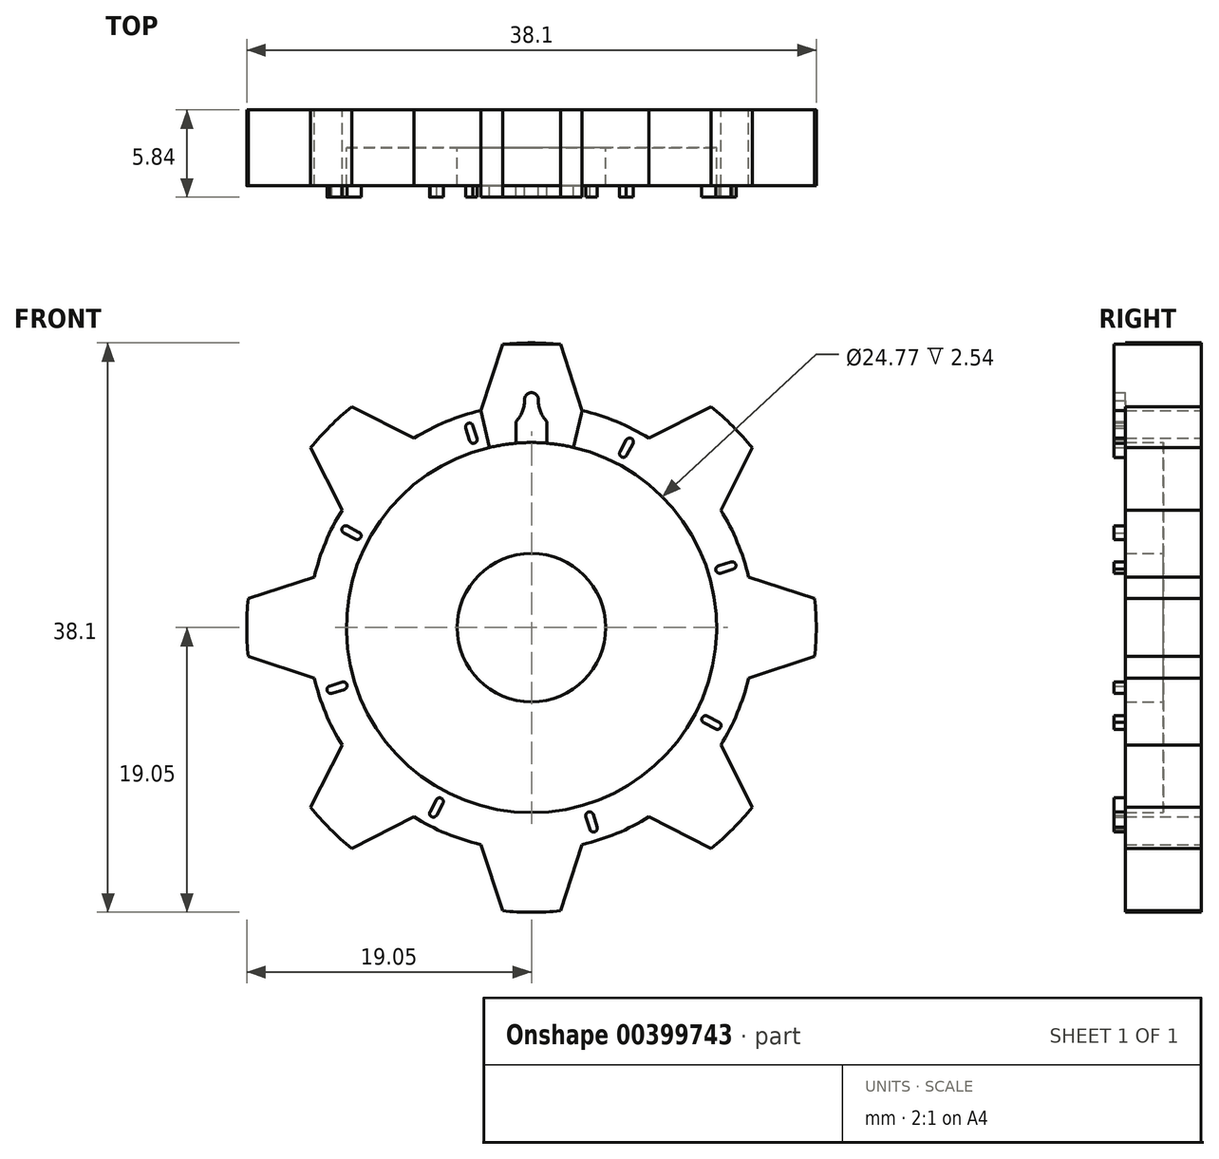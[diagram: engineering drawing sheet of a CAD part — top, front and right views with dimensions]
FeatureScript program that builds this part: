
annotation { "Feature Type Name" : "Feature", "Feature Type Description" : "" }
export const myFeature = defineFeature(function(context is Context, id is Id, definition is map)
    precondition{}
    {
        {
            var Q0;
            Q0=qCreatedBy(makeId("Front.planeOp"),FACE);
            var sketch = newSketch(context, id + "F0", { "sketchPlane" : qUnion([Q0])});
            skCircle(sketch, "E0", {"center": v(0, 0) * mm, "radius": 19.05 * mm});
            skLineSegment(sketch, "E1", {"start": v(-1.9, 19.05) * mm, "end": v(1.9, 19.05) * mm});
            skPoint(sketch, "E2", {"position": v(0, 19.05) * mm});
            skLineSegment(sketch, "E3.1.0", {"start": v(-14.82, 12.12) * mm, "end": v(-12.12, 14.82) * mm});
            skLineSegment(sketch, "E3.2.0", {"start": v(-19.05, -1.9) * mm, "end": v(-19.05, 1.9) * mm});
            skLineSegment(sketch, "E4.1.3.0", {"start": v(-12.12, -14.82) * mm, "end": v(-14.82, -12.12) * mm});
            skLineSegment(sketch, "E4.1.4.0", {"start": v(1.9, -19.05) * mm, "end": v(-1.9, -19.05) * mm});
            skLineSegment(sketch, "E4.1.5.0", {"start": v(14.82, -12.12) * mm, "end": v(12.12, -14.82) * mm});
            skLineSegment(sketch, "E4.1.6.0", {"start": v(19.05, 1.9) * mm, "end": v(19.05, -1.9) * mm});
            skLineSegment(sketch, "E4.1.7.0", {"start": v(12.12, 14.82) * mm, "end": v(14.82, 12.12) * mm});
            skCircle(sketch, "E5", {"center": v(0, 0) * mm, "radius": 14.91 * mm});
            skLineSegment(sketch, "E6", {"start": v(-1.9, 19.05) * mm, "end": v(-3.4, 14.52) * mm});
            skLineSegment(sketch, "E7", {"start": v(0, 0) * mm, "end": v(0, 23.52) * mm});
            skLineSegment(sketch, "E8.MirrorCS", {"start": v(1.9, 19.05) * mm, "end": v(3.4, 14.52) * mm});
            skLineSegment(sketch, "E9.1.0", {"start": v(-14.82, 12.12) * mm, "end": v(-12.67, 7.87) * mm});
            skLineSegment(sketch, "E9.1.1", {"start": v(-12.12, 14.82) * mm, "end": v(-7.87, 12.67) * mm});
            skLineSegment(sketch, "E9.2.0", {"start": v(-19.05, -1.9) * mm, "end": v(-14.52, -3.4) * mm});
            skLineSegment(sketch, "E9.2.1", {"start": v(-19.05, 1.9) * mm, "end": v(-14.52, 3.4) * mm});
            skLineSegment(sketch, "E9.3.0", {"start": v(-12.12, -14.82) * mm, "end": v(-7.87, -12.67) * mm});
            skLineSegment(sketch, "E9.3.1", {"start": v(-14.82, -12.12) * mm, "end": v(-12.67, -7.87) * mm});
            skLineSegment(sketch, "E9.4.0", {"start": v(1.9, -19.05) * mm, "end": v(3.4, -14.52) * mm});
            skLineSegment(sketch, "E9.4.1", {"start": v(-1.9, -19.05) * mm, "end": v(-3.4, -14.52) * mm});
            skLineSegment(sketch, "E9.5.0", {"start": v(14.82, -12.12) * mm, "end": v(12.67, -7.87) * mm});
            skLineSegment(sketch, "E9.5.1", {"start": v(12.12, -14.82) * mm, "end": v(7.87, -12.67) * mm});
            skLineSegment(sketch, "E9.6.0", {"start": v(19.05, 1.9) * mm, "end": v(14.52, 3.4) * mm});
            skLineSegment(sketch, "E9.6.1", {"start": v(19.05, -1.9) * mm, "end": v(14.52, -3.4) * mm});
            skLineSegment(sketch, "E9.7.0", {"start": v(12.12, 14.82) * mm, "end": v(7.87, 12.67) * mm});
            skLineSegment(sketch, "E9.7.1", {"start": v(14.82, 12.12) * mm, "end": v(12.67, 7.87) * mm});
            skSolve(sketch);
        }
        {
            var Q0;
            {var subQ3=sQuery(id+"F0.wireOp",EDGE,"E9.1.1");var subQ5=sQuery(id+"F0.wireOp",EDGE,"E0");var subQ8=makeQuery(id+"F0.imprint","INTERSECT",VERTEX,{"derivedFrom":[subQ5,subQ3]});Q0=makeQuery(id+"F0.imprint","IMPRINT",FACE,{"disambiguationData":[TD([[makeQuery(id+"F0.imprint","IMPRINT",EDGE,{"disambiguationData":[TD([[subQ8,-1.0]])],"derivedFrom":subQ5}),1.0]])]});}
            var Q1;
            {var subQ3=sQuery(id+"F0.wireOp",EDGE,"E9.7.1");var subQ5=sQuery(id+"F0.wireOp",EDGE,"E0");var subQ8=makeQuery(id+"F0.imprint","INTERSECT",VERTEX,{"derivedFrom":[subQ5,subQ3]});Q1=makeQuery(id+"F0.imprint","IMPRINT",FACE,{"disambiguationData":[TD([[makeQuery(id+"F0.imprint","IMPRINT",EDGE,{"disambiguationData":[TD([[subQ8,-1.0]])],"derivedFrom":subQ5}),1.0]])]});}
            var Q2;
            {var subQ0=sQuery(id+"F0.wireOp",EDGE,"E9.6.0");var subQ5=sQuery(id+"F0.wireOp",EDGE,"E0");var subQ8=makeQuery(id+"F0.imprint","INTERSECT",VERTEX,{"derivedFrom":[subQ5,subQ0]});Q2=makeQuery(id+"F0.imprint","IMPRINT",FACE,{"disambiguationData":[TD([[makeQuery(id+"F0.imprint","IMPRINT",EDGE,{"disambiguationData":[TD([[subQ8,1.0]])],"derivedFrom":subQ5}),1.0]])]});}
            var Q3;
            {var subQ0=sQuery(id+"F0.wireOp",EDGE,"E8.MirrorCS");var subQ5=sQuery(id+"F0.wireOp",EDGE,"E5");var subQ6=makeQuery(id+"F0.imprint","INTERSECT",VERTEX,{"derivedFrom":[subQ5,subQ0]});Q3=makeQuery(id+"F0.imprint","IMPRINT",FACE,{"disambiguationData":[TD([[makeQuery(id+"F0.imprint","IMPRINT",EDGE,{"disambiguationData":[TD([[subQ6,-1.0]])],"derivedFrom":subQ5}),-1.0]])]});}
            var Q4;
            {var subQ0=sQuery(id+"F0.wireOp",EDGE,"E6");var subQ5=sQuery(id+"F0.wireOp",EDGE,"E5");var subQ6=makeQuery(id+"F0.imprint","INTERSECT",VERTEX,{"derivedFrom":[subQ5,subQ0]});Q4=makeQuery(id+"F0.imprint","IMPRINT",FACE,{"disambiguationData":[TD([[makeQuery(id+"F0.imprint","IMPRINT",EDGE,{"disambiguationData":[TD([[subQ6,1.0]])],"derivedFrom":subQ5}),-1.0]])]});}
            var Q5;
            {var subQ3=sQuery(id+"F0.wireOp",EDGE,"E9.2.1");var subQ5=sQuery(id+"F0.wireOp",EDGE,"E0");var subQ8=makeQuery(id+"F0.imprint","INTERSECT",VERTEX,{"derivedFrom":[subQ5,subQ3]});Q5=makeQuery(id+"F0.imprint","IMPRINT",FACE,{"disambiguationData":[TD([[makeQuery(id+"F0.imprint","IMPRINT",EDGE,{"disambiguationData":[TD([[subQ8,-1.0]])],"derivedFrom":subQ5}),1.0]])]});}
            var Q6;
            {var subQ3=sQuery(id+"F0.wireOp",EDGE,"E0");var subQ5=sQuery(id+"F0.wireOp",EDGE,"E9.3.1");var subQ8=makeQuery(id+"F0.imprint","INTERSECT",VERTEX,{"derivedFrom":[subQ3,subQ5]});Q6=makeQuery(id+"F0.imprint","IMPRINT",FACE,{"disambiguationData":[TD([[makeQuery(id+"F0.imprint","IMPRINT",EDGE,{"disambiguationData":[TD([[subQ8,-1.0]])],"derivedFrom":subQ3}),1.0]])]});}
            var Q7;
            {var subQ3=sQuery(id+"F0.wireOp",EDGE,"E0");var subQ6=sQuery(id+"F0.wireOp",EDGE,"E9.4.1");var subQ8=makeQuery(id+"F0.imprint","INTERSECT",VERTEX,{"derivedFrom":[subQ3,subQ6]});Q7=makeQuery(id+"F0.imprint","IMPRINT",FACE,{"disambiguationData":[TD([[makeQuery(id+"F0.imprint","IMPRINT",EDGE,{"disambiguationData":[TD([[subQ8,-1.0]])],"derivedFrom":subQ3}),1.0]])]});}
            var Q8;
            {var subQ3=sQuery(id+"F0.wireOp",EDGE,"E0");var subQ5=sQuery(id+"F0.wireOp",EDGE,"E9.5.1");var subQ8=makeQuery(id+"F0.imprint","INTERSECT",VERTEX,{"derivedFrom":[subQ3,subQ5]});Q8=makeQuery(id+"F0.imprint","IMPRINT",FACE,{"disambiguationData":[TD([[makeQuery(id+"F0.imprint","IMPRINT",EDGE,{"disambiguationData":[TD([[subQ8,-1.0]])],"derivedFrom":subQ3}),1.0]])]});}
            var Q9;
            {var subQ0=sQuery(id+"F0.wireOp",EDGE,"E5");var subQ8=makeQuery(id+"F0.imprint","INTERSECT",VERTEX,{"derivedFrom":[subQ0,sQuery(id+"F0.wireOp",EDGE,"E9.6.0")]});Q9=makeQuery(id+"F0.imprint","IMPRINT",FACE,{"disambiguationData":[TD([[makeQuery(id+"F0.imprint","IMPRINT",EDGE,{"disambiguationData":[TD([[subQ8,-1.0]])],"derivedFrom":subQ0}),1.0]])]});}
            extrude(context, id + "F1", {"entities" : qUnion([Q0, Q1, Q2, Q3, Q4, Q5, Q6, Q7, Q8, Q9]), "depth" : 2.54 * mm});
        }
        {
            var Q0;
            Q0=makeQuery(id+"F1.opExtrude","CAP_FACE",FACE,{"disambiguationData":[OSD([sQuery(id+"F0.wireOp",EDGE,"E0"),sQuery(id+"F0.wireOp",EDGE,"E5"),sQuery(id+"F0.wireOp",EDGE,"E6"),sQuery(id+"F0.wireOp",EDGE,"E8.MirrorCS"),sQuery(id+"F0.wireOp",EDGE,"E9.1.0"),sQuery(id+"F0.wireOp",EDGE,"E9.1.1"),sQuery(id+"F0.wireOp",EDGE,"E9.2.0"),sQuery(id+"F0.wireOp",EDGE,"E9.2.1"),sQuery(id+"F0.wireOp",EDGE,"E9.3.0"),sQuery(id+"F0.wireOp",EDGE,"E9.3.1"),sQuery(id+"F0.wireOp",EDGE,"E9.4.0"),sQuery(id+"F0.wireOp",EDGE,"E9.4.1"),sQuery(id+"F0.wireOp",EDGE,"E9.5.0"),sQuery(id+"F0.wireOp",EDGE,"E9.5.1"),sQuery(id+"F0.wireOp",EDGE,"E9.6.0"),sQuery(id+"F0.wireOp",EDGE,"E9.6.1"),sQuery(id+"F0.wireOp",EDGE,"E9.7.0"),sQuery(id+"F0.wireOp",EDGE,"E9.7.1")])],"isStart":false});
            var sketch = newSketch(context, id + "F2", { "sketchPlane" : qUnion([Q0])});
            skCircle(sketch, "E10", {"center": v(0, 0) * mm, "radius": 12.38 * mm});
            skCircle(sketch, "E11", {"center": v(0, 0) * mm, "radius": 4.97 * mm});
            skSolve(sketch);
        }
        {
            var Q0;
            Q0=makeQuery(id+"F2.imprint","IMPRINT",FACE,{"disambiguationData":[TD([[makeQuery(id+"F2.imprint","IMPRINT",EDGE,{"derivedFrom":sQuery(id+"F2.wireOp",EDGE,"E10")}),-1.0]])]});
            var Q1;
            Q1=makeQuery(id+"F2.imprint","IMPRINT",FACE,{"disambiguationData":[TD([[makeQuery(id+"F2.imprint","IMPRINT",EDGE,{"derivedFrom":sQuery(id+"F2.wireOp",EDGE,"E11")}),1.0]])]});
            extrude(context, id + "F3", {"entities" : qUnion([Q0, Q1]), "operationType" : NewBodyOperationType.ADD, "depth" : 2.54 * mm});
        }
        {
            var Q0;
            Q0=makeQuery(id+"F3.opExtrude","CAP_FACE",FACE,{"disambiguationData":[OSD([sQuery(id+"F2.wireOp",EDGE,"E11")])],"isStart":false});
            var sketch = newSketch(context, id + "F4", { "sketchPlane" : qUnion([Q0])});
            skCircle(sketch, "E12", {"center": v(0, 0) * mm, "radius": 2.8 * mm});
            skPoint(sketch, "E13", {"position": v(-1.94, 18.95) * mm});
            skPoint(sketch, "E14", {"position": v(1.94, 18.95) * mm});
            skPoint(sketch, "E15", {"position": v(-3.4, 14.52) * mm});
            skPoint(sketch, "E16", {"position": v(3.4, 14.52) * mm});
            skLineSegment(sketch, "E17", {"start": v(-3.4, 14.52) * mm, "end": v(-1.94, 18.95) * mm});
            skLineSegment(sketch, "E18", {"start": v(1.94, 18.95) * mm, "end": v(3.4, 14.52) * mm});
            skLineSegment(sketch, "E19", {"start": v(-3.4, 14.52) * mm, "end": v(-2.81, 12.05) * mm});
            skLineSegment(sketch, "E20", {"start": v(3.4, 14.52) * mm, "end": v(2.8, 12.06) * mm});
            skArc(sketch, "E21", {"start": v(2.8, 12.06) * mm, "mid": v(1.91, 12.23) * mm, "end": v(1, 12.33) * mm});
            skLineSegment(sketch, "E22", {"start": v(-1.94, 18.95) * mm, "end": v(1.94, 18.95) * mm});
            skLineSegment(sketch, "E23", {"start": v(0, 0) * mm, "end": v(0, 11.5) * mm, "construction": true});
            skPoint(sketch, "E23.endSnap0", {"position": v(0, 12.37) * mm});
            skArc(sketch, "E24", {"start": v(-3.9, 13.49) * mm, "mid": v(-4.22, 13.67) * mm, "end": v(-4.4, 13.35) * mm});
            skArc(sketch, "E25", {"start": v(-4.13, 12.5) * mm, "mid": v(-3.81, 12.34) * mm, "end": v(-3.65, 12.66) * mm});
            skLineSegment(sketch, "E26", {"start": v(0, 0) * mm, "end": v(-4.15, 13.43) * mm, "construction": true});
            skLineSegment(sketch, "E27", {"start": v(-4.4, 13.35) * mm, "end": v(-4.13, 12.5) * mm});
            skLineSegment(sketch, "E28", {"start": v(-3.91, 13.52) * mm, "end": v(-3.65, 12.66) * mm});
            skLineSegment(sketch, "E29.MirrorCS", {"start": v(3.91, 13.52) * mm, "end": v(3.65, 12.66) * mm});
            skArc(sketch, "E30.MirrorCS", {"start": v(3.9, 13.49) * mm, "mid": v(4.22, 13.67) * mm, "end": v(4.4, 13.35) * mm});
            skArc(sketch, "E31.MirrorCS", {"start": v(4.13, 12.5) * mm, "mid": v(3.81, 12.34) * mm, "end": v(3.65, 12.66) * mm});
            skLineSegment(sketch, "E32.MirrorCS", {"start": v(4.4, 13.35) * mm, "end": v(4.13, 12.5) * mm});
            skArc(sketch, "E33", {"start": v(0.46, 15.2) * mm, "mid": v(0, 15.72) * mm, "end": v(-0.46, 15.2) * mm});
            skLineSegment(sketch, "E34", {"start": v(1, 13.79) * mm, "end": v(1, 12.33) * mm});
            skLineSegment(sketch, "E35", {"start": v(-1.03, 13.79) * mm, "end": v(-1.03, 12.33) * mm});
            skArc(sketch, "E36", {"start": v(-1.03, 13.79) * mm, "mid": v(-0.6, 14.48) * mm, "end": v(-0.46, 15.3) * mm});
            skArc(sketch, "E37.MirrorCS", {"start": v(1.03, 13.79) * mm, "mid": v(0.6, 14.48) * mm, "end": v(0.46, 15.3) * mm});
            skPoint(sketch, "E38.start.orphan", {"position": v(0, 13.79) * mm});
            skArc(sketch, "E39.trimOffspring", {"start": v(-1.03, 12.33) * mm, "mid": v(-1.93, 12.22) * mm, "end": v(-2.81, 12.05) * mm});
            skLineSegment(sketch, "E40.MirrorCS", {"start": v(1.03, 13.79) * mm, "end": v(1.03, 12.33) * mm});
            skArc(sketch, "E41.MirrorCS", {"start": v(1.03, 12.33) * mm, "mid": v(1.92, 12.22) * mm, "end": v(2.81, 12.05) * mm});
            skLineSegment(sketch, "E42.MirrorCS", {"start": v(3.4, 14.52) * mm, "end": v(2.81, 12.05) * mm});
            skLineSegment(sketch, "E43.MirrorCS", {"start": v(3.4, 14.52) * mm, "end": v(1.94, 18.95) * mm});
            skArc(sketch, "E44.MirrorCS", {"start": v(-0.46, 15.2) * mm, "mid": v(0, 15.72) * mm, "end": v(0.46, 15.2) * mm});
            skLineSegment(sketch, "E45.1.0", {"start": v(-12.55, 6.34) * mm, "end": v(-11.77, 5.92) * mm});
            skArc(sketch, "E45.1.1", {"start": v(-12.3, 6.78) * mm, "mid": v(-12.65, 6.69) * mm, "end": v(-12.55, 6.34) * mm});
            skLineSegment(sketch, "E45.1.2", {"start": v(-12.33, 6.8) * mm, "end": v(-11.53, 6.37) * mm});
            skArc(sketch, "E45.1.3", {"start": v(-11.77, 5.92) * mm, "mid": v(-11.42, 6.03) * mm, "end": v(-11.53, 6.37) * mm});
            skLineSegment(sketch, "E45.1.4", {"start": v(-12.67, 7.87) * mm, "end": v(-10.51, 6.53) * mm});
            skArc(sketch, "E45.1.5", {"start": v(-9.45, 8) * mm, "mid": v(-10, 7.28) * mm, "end": v(-10.51, 6.53) * mm});
            skLineSegment(sketch, "E45.1.6", {"start": v(-10.47, 9.02) * mm, "end": v(-9.45, 8) * mm});
            skArc(sketch, "E45.1.7", {"start": v(-10.47, 9.02) * mm, "mid": v(-10.66, 9.82) * mm, "end": v(-11.14, 10.49) * mm});
            skArc(sketch, "E45.1.8", {"start": v(-10.42, 11.07) * mm, "mid": v(-11.11, 11.12) * mm, "end": v(-11.08, 10.42) * mm});
            skArc(sketch, "E45.1.9", {"start": v(-9.02, 10.47) * mm, "mid": v(-9.82, 10.66) * mm, "end": v(-10.49, 11.14) * mm});
            skLineSegment(sketch, "E45.1.10", {"start": v(-9.02, 10.47) * mm, "end": v(-8, 9.44) * mm});
            skArc(sketch, "E45.1.11", {"start": v(-8, 9.44) * mm, "mid": v(-7.28, 10) * mm, "end": v(-6.53, 10.51) * mm});
            skLineSegment(sketch, "E45.1.12", {"start": v(-7.87, 12.67) * mm, "end": v(-6.54, 10.5) * mm});
            skArc(sketch, "E45.1.13", {"start": v(-5.92, 11.77) * mm, "mid": v(-6.03, 11.42) * mm, "end": v(-6.37, 11.53) * mm});
            skArc(sketch, "E45.1.14", {"start": v(-6.78, 12.3) * mm, "mid": v(-6.69, 12.65) * mm, "end": v(-6.34, 12.55) * mm});
            skLineSegment(sketch, "E45.1.15", {"start": v(-6.34, 12.55) * mm, "end": v(-5.92, 11.77) * mm});
            skLineSegment(sketch, "E45.1.16", {"start": v(-6.8, 12.33) * mm, "end": v(-6.37, 11.53) * mm});
            skLineSegment(sketch, "E45.1.17", {"start": v(-7.87, 12.67) * mm, "end": v(-12.03, 14.77) * mm});
            skLineSegment(sketch, "E45.1.18", {"start": v(-14.77, 12.03) * mm, "end": v(-12.03, 14.77) * mm});
            skLineSegment(sketch, "E45.1.19", {"start": v(-12.67, 7.87) * mm, "end": v(-14.77, 12.03) * mm});
            skLineSegment(sketch, "E45.2.0", {"start": v(-13.35, -4.4) * mm, "end": v(-12.5, -4.13) * mm});
            skArc(sketch, "E45.2.1", {"start": v(-13.49, -3.9) * mm, "mid": v(-13.67, -4.22) * mm, "end": v(-13.35, -4.4) * mm});
            skLineSegment(sketch, "E45.2.2", {"start": v(-13.52, -3.91) * mm, "end": v(-12.66, -3.65) * mm});
            skArc(sketch, "E45.2.3", {"start": v(-12.5, -4.13) * mm, "mid": v(-12.34, -3.81) * mm, "end": v(-12.66, -3.65) * mm});
            skLineSegment(sketch, "E45.2.4", {"start": v(-14.52, -3.4) * mm, "end": v(-12.05, -2.81) * mm});
            skArc(sketch, "E45.2.5", {"start": v(-12.33, -1.03) * mm, "mid": v(-12.22, -1.93) * mm, "end": v(-12.05, -2.81) * mm});
            skLineSegment(sketch, "E45.2.6", {"start": v(-13.79, -1.03) * mm, "end": v(-12.33, -1.03) * mm});
            skArc(sketch, "E45.2.7", {"start": v(-13.79, -1.03) * mm, "mid": v(-14.48, -0.6) * mm, "end": v(-15.3, -0.46) * mm});
            skArc(sketch, "E45.2.8", {"start": v(-15.2, 0.46) * mm, "mid": v(-15.72, 0) * mm, "end": v(-15.2, -0.46) * mm});
            skArc(sketch, "E45.2.9", {"start": v(-13.79, 1.03) * mm, "mid": v(-14.48, 0.6) * mm, "end": v(-15.3, 0.46) * mm});
            skLineSegment(sketch, "E45.2.10", {"start": v(-13.79, 1.03) * mm, "end": v(-12.33, 1.03) * mm});
            skArc(sketch, "E45.2.11", {"start": v(-12.33, 1.03) * mm, "mid": v(-12.22, 1.92) * mm, "end": v(-12.05, 2.81) * mm});
            skLineSegment(sketch, "E45.2.12", {"start": v(-14.52, 3.4) * mm, "end": v(-12.06, 2.8) * mm});
            skArc(sketch, "E45.2.13", {"start": v(-12.5, 4.13) * mm, "mid": v(-12.34, 3.81) * mm, "end": v(-12.66, 3.65) * mm});
            skArc(sketch, "E45.2.14", {"start": v(-13.49, 3.9) * mm, "mid": v(-13.67, 4.22) * mm, "end": v(-13.35, 4.4) * mm});
            skLineSegment(sketch, "E45.2.15", {"start": v(-13.35, 4.4) * mm, "end": v(-12.5, 4.13) * mm});
            skLineSegment(sketch, "E45.2.16", {"start": v(-13.52, 3.91) * mm, "end": v(-12.66, 3.65) * mm});
            skLineSegment(sketch, "E45.2.17", {"start": v(-14.52, 3.4) * mm, "end": v(-18.95, 1.94) * mm});
            skLineSegment(sketch, "E45.2.18", {"start": v(-18.95, -1.94) * mm, "end": v(-18.95, 1.94) * mm});
            skLineSegment(sketch, "E45.2.19", {"start": v(-14.52, -3.4) * mm, "end": v(-18.95, -1.94) * mm});
            skLineSegment(sketch, "E46.2.3.0", {"start": v(-6.34, -12.55) * mm, "end": v(-5.92, -11.77) * mm});
            skArc(sketch, "E46.3.3.0", {"start": v(-6.78, -12.3) * mm, "mid": v(-6.69, -12.65) * mm, "end": v(-6.34, -12.55) * mm});
            skLineSegment(sketch, "E46.7.3.0", {"start": v(-6.8, -12.33) * mm, "end": v(-6.37, -11.53) * mm});
            skArc(sketch, "E46.10.3.0", {"start": v(-5.92, -11.77) * mm, "mid": v(-6.03, -11.42) * mm, "end": v(-6.37, -11.53) * mm});
            skLineSegment(sketch, "E46.14.3.0", {"start": v(-7.87, -12.67) * mm, "end": v(-6.53, -10.51) * mm});
            skArc(sketch, "E46.17.3.0", {"start": v(-8, -9.45) * mm, "mid": v(-7.28, -10) * mm, "end": v(-6.53, -10.51) * mm});
            skLineSegment(sketch, "E46.21.3.0", {"start": v(-9.02, -10.47) * mm, "end": v(-8, -9.45) * mm});
            skArc(sketch, "E46.24.3.0", {"start": v(-9.02, -10.47) * mm, "mid": v(-9.82, -10.66) * mm, "end": v(-10.49, -11.14) * mm});
            skArc(sketch, "E46.28.3.0", {"start": v(-11.07, -10.42) * mm, "mid": v(-11.12, -11.11) * mm, "end": v(-10.42, -11.08) * mm});
            skArc(sketch, "E46.32.3.0", {"start": v(-10.47, -9.02) * mm, "mid": v(-10.66, -9.82) * mm, "end": v(-11.14, -10.49) * mm});
            skLineSegment(sketch, "E46.36.3.0", {"start": v(-10.47, -9.02) * mm, "end": v(-9.44, -8) * mm});
            skArc(sketch, "E46.39.3.0", {"start": v(-9.44, -8) * mm, "mid": v(-10, -7.28) * mm, "end": v(-10.51, -6.53) * mm});
            skLineSegment(sketch, "E46.43.3.0", {"start": v(-12.67, -7.87) * mm, "end": v(-10.5, -6.54) * mm});
            skArc(sketch, "E46.46.3.0", {"start": v(-11.77, -5.92) * mm, "mid": v(-11.42, -6.03) * mm, "end": v(-11.53, -6.37) * mm});
            skArc(sketch, "E46.50.3.0", {"start": v(-12.3, -6.78) * mm, "mid": v(-12.65, -6.69) * mm, "end": v(-12.55, -6.34) * mm});
            skLineSegment(sketch, "E46.54.3.0", {"start": v(-12.55, -6.34) * mm, "end": v(-11.77, -5.92) * mm});
            skLineSegment(sketch, "E46.57.3.0", {"start": v(-12.33, -6.8) * mm, "end": v(-11.53, -6.37) * mm});
            skLineSegment(sketch, "E46.60.3.0", {"start": v(-12.67, -7.87) * mm, "end": v(-14.77, -12.03) * mm});
            skLineSegment(sketch, "E46.63.3.0", {"start": v(-12.03, -14.77) * mm, "end": v(-14.77, -12.03) * mm});
            skLineSegment(sketch, "E46.66.3.0", {"start": v(-7.87, -12.67) * mm, "end": v(-12.03, -14.77) * mm});
            skLineSegment(sketch, "E46.2.4.0", {"start": v(4.4, -13.35) * mm, "end": v(4.13, -12.5) * mm});
            skArc(sketch, "E46.3.4.0", {"start": v(3.9, -13.49) * mm, "mid": v(4.22, -13.67) * mm, "end": v(4.4, -13.35) * mm});
            skLineSegment(sketch, "E46.7.4.0", {"start": v(3.91, -13.52) * mm, "end": v(3.65, -12.66) * mm});
            skArc(sketch, "E46.10.4.0", {"start": v(4.13, -12.5) * mm, "mid": v(3.81, -12.34) * mm, "end": v(3.65, -12.66) * mm});
            skLineSegment(sketch, "E46.14.4.0", {"start": v(3.4, -14.52) * mm, "end": v(2.81, -12.05) * mm});
            skArc(sketch, "E46.17.4.0", {"start": v(1.03, -12.33) * mm, "mid": v(1.93, -12.22) * mm, "end": v(2.81, -12.05) * mm});
            skLineSegment(sketch, "E46.21.4.0", {"start": v(1.03, -13.79) * mm, "end": v(1.03, -12.33) * mm});
            skArc(sketch, "E46.24.4.0", {"start": v(1.03, -13.79) * mm, "mid": v(0.6, -14.48) * mm, "end": v(0.46, -15.3) * mm});
            skArc(sketch, "E46.28.4.0", {"start": v(-0.46, -15.2) * mm, "mid": v(0, -15.72) * mm, "end": v(0.46, -15.2) * mm});
            skArc(sketch, "E46.32.4.0", {"start": v(-1.03, -13.79) * mm, "mid": v(-0.6, -14.48) * mm, "end": v(-0.46, -15.3) * mm});
            skLineSegment(sketch, "E46.36.4.0", {"start": v(-1.03, -13.79) * mm, "end": v(-1.03, -12.33) * mm});
            skArc(sketch, "E46.39.4.0", {"start": v(-1.03, -12.33) * mm, "mid": v(-1.92, -12.22) * mm, "end": v(-2.81, -12.05) * mm});
            skLineSegment(sketch, "E46.43.4.0", {"start": v(-3.4, -14.52) * mm, "end": v(-2.8, -12.06) * mm});
            skArc(sketch, "E46.46.4.0", {"start": v(-4.13, -12.5) * mm, "mid": v(-3.81, -12.34) * mm, "end": v(-3.65, -12.66) * mm});
            skArc(sketch, "E46.50.4.0", {"start": v(-3.9, -13.49) * mm, "mid": v(-4.22, -13.67) * mm, "end": v(-4.4, -13.35) * mm});
            skLineSegment(sketch, "E46.54.4.0", {"start": v(-4.4, -13.35) * mm, "end": v(-4.13, -12.5) * mm});
            skLineSegment(sketch, "E46.57.4.0", {"start": v(-3.91, -13.52) * mm, "end": v(-3.65, -12.66) * mm});
            skLineSegment(sketch, "E46.60.4.0", {"start": v(-3.4, -14.52) * mm, "end": v(-1.94, -18.95) * mm});
            skLineSegment(sketch, "E46.63.4.0", {"start": v(1.94, -18.95) * mm, "end": v(-1.94, -18.95) * mm});
            skLineSegment(sketch, "E46.66.4.0", {"start": v(3.4, -14.52) * mm, "end": v(1.94, -18.95) * mm});
            skLineSegment(sketch, "E46.2.5.0", {"start": v(12.55, -6.34) * mm, "end": v(11.77, -5.92) * mm});
            skArc(sketch, "E46.3.5.0", {"start": v(12.3, -6.78) * mm, "mid": v(12.65, -6.69) * mm, "end": v(12.55, -6.34) * mm});
            skLineSegment(sketch, "E46.7.5.0", {"start": v(12.33, -6.8) * mm, "end": v(11.53, -6.37) * mm});
            skArc(sketch, "E46.10.5.0", {"start": v(11.77, -5.92) * mm, "mid": v(11.42, -6.03) * mm, "end": v(11.53, -6.37) * mm});
            skLineSegment(sketch, "E46.14.5.0", {"start": v(12.67, -7.87) * mm, "end": v(10.51, -6.53) * mm});
            skArc(sketch, "E46.17.5.0", {"start": v(9.45, -8) * mm, "mid": v(10, -7.28) * mm, "end": v(10.51, -6.53) * mm});
            skLineSegment(sketch, "E46.21.5.0", {"start": v(10.47, -9.02) * mm, "end": v(9.45, -8) * mm});
            skArc(sketch, "E46.24.5.0", {"start": v(10.47, -9.02) * mm, "mid": v(10.66, -9.82) * mm, "end": v(11.14, -10.49) * mm});
            skArc(sketch, "E46.28.5.0", {"start": v(10.42, -11.07) * mm, "mid": v(11.11, -11.12) * mm, "end": v(11.08, -10.42) * mm});
            skArc(sketch, "E46.32.5.0", {"start": v(9.02, -10.47) * mm, "mid": v(9.82, -10.66) * mm, "end": v(10.49, -11.14) * mm});
            skLineSegment(sketch, "E46.36.5.0", {"start": v(9.02, -10.47) * mm, "end": v(8, -9.44) * mm});
            skArc(sketch, "E46.39.5.0", {"start": v(8, -9.44) * mm, "mid": v(7.28, -10) * mm, "end": v(6.53, -10.51) * mm});
            skLineSegment(sketch, "E46.43.5.0", {"start": v(7.87, -12.67) * mm, "end": v(6.54, -10.5) * mm});
            skArc(sketch, "E46.46.5.0", {"start": v(5.92, -11.77) * mm, "mid": v(6.03, -11.42) * mm, "end": v(6.37, -11.53) * mm});
            skArc(sketch, "E46.50.5.0", {"start": v(6.78, -12.3) * mm, "mid": v(6.69, -12.65) * mm, "end": v(6.34, -12.55) * mm});
            skLineSegment(sketch, "E46.54.5.0", {"start": v(6.34, -12.55) * mm, "end": v(5.92, -11.77) * mm});
            skLineSegment(sketch, "E46.57.5.0", {"start": v(6.8, -12.33) * mm, "end": v(6.37, -11.53) * mm});
            skLineSegment(sketch, "E46.60.5.0", {"start": v(7.87, -12.67) * mm, "end": v(12.03, -14.77) * mm});
            skLineSegment(sketch, "E46.63.5.0", {"start": v(14.77, -12.03) * mm, "end": v(12.03, -14.77) * mm});
            skLineSegment(sketch, "E46.66.5.0", {"start": v(12.67, -7.87) * mm, "end": v(14.77, -12.03) * mm});
            skLineSegment(sketch, "E46.2.6.0", {"start": v(13.35, 4.4) * mm, "end": v(12.5, 4.13) * mm});
            skArc(sketch, "E46.3.6.0", {"start": v(13.49, 3.9) * mm, "mid": v(13.67, 4.22) * mm, "end": v(13.35, 4.4) * mm});
            skLineSegment(sketch, "E46.7.6.0", {"start": v(13.52, 3.91) * mm, "end": v(12.66, 3.65) * mm});
            skArc(sketch, "E46.10.6.0", {"start": v(12.5, 4.13) * mm, "mid": v(12.34, 3.81) * mm, "end": v(12.66, 3.65) * mm});
            skLineSegment(sketch, "E46.14.6.0", {"start": v(14.52, 3.4) * mm, "end": v(12.05, 2.81) * mm});
            skArc(sketch, "E46.17.6.0", {"start": v(12.33, 1.03) * mm, "mid": v(12.22, 1.93) * mm, "end": v(12.05, 2.81) * mm});
            skLineSegment(sketch, "E46.21.6.0", {"start": v(13.79, 1.03) * mm, "end": v(12.33, 1.03) * mm});
            skArc(sketch, "E46.24.6.0", {"start": v(13.79, 1.03) * mm, "mid": v(14.48, 0.6) * mm, "end": v(15.3, 0.46) * mm});
            skArc(sketch, "E46.28.6.0", {"start": v(15.2, -0.46) * mm, "mid": v(15.72, 0) * mm, "end": v(15.2, 0.46) * mm});
            skArc(sketch, "E46.32.6.0", {"start": v(13.79, -1.03) * mm, "mid": v(14.48, -0.6) * mm, "end": v(15.3, -0.46) * mm});
            skLineSegment(sketch, "E46.36.6.0", {"start": v(13.79, -1.03) * mm, "end": v(12.33, -1.03) * mm});
            skArc(sketch, "E46.39.6.0", {"start": v(12.33, -1.03) * mm, "mid": v(12.22, -1.92) * mm, "end": v(12.05, -2.81) * mm});
            skLineSegment(sketch, "E46.43.6.0", {"start": v(14.52, -3.4) * mm, "end": v(12.06, -2.8) * mm});
            skArc(sketch, "E46.46.6.0", {"start": v(12.5, -4.13) * mm, "mid": v(12.34, -3.81) * mm, "end": v(12.66, -3.65) * mm});
            skArc(sketch, "E46.50.6.0", {"start": v(13.49, -3.9) * mm, "mid": v(13.67, -4.22) * mm, "end": v(13.35, -4.4) * mm});
            skLineSegment(sketch, "E46.54.6.0", {"start": v(13.35, -4.4) * mm, "end": v(12.5, -4.13) * mm});
            skLineSegment(sketch, "E46.57.6.0", {"start": v(13.52, -3.91) * mm, "end": v(12.66, -3.65) * mm});
            skLineSegment(sketch, "E46.60.6.0", {"start": v(14.52, -3.4) * mm, "end": v(18.95, -1.94) * mm});
            skLineSegment(sketch, "E46.63.6.0", {"start": v(18.95, 1.94) * mm, "end": v(18.95, -1.94) * mm});
            skLineSegment(sketch, "E46.66.6.0", {"start": v(14.52, 3.4) * mm, "end": v(18.95, 1.94) * mm});
            skLineSegment(sketch, "E46.2.7.0", {"start": v(6.34, 12.55) * mm, "end": v(5.92, 11.77) * mm});
            skArc(sketch, "E46.3.7.0", {"start": v(6.78, 12.3) * mm, "mid": v(6.69, 12.65) * mm, "end": v(6.34, 12.55) * mm});
            skLineSegment(sketch, "E46.7.7.0", {"start": v(6.8, 12.33) * mm, "end": v(6.37, 11.53) * mm});
            skArc(sketch, "E46.10.7.0", {"start": v(5.92, 11.77) * mm, "mid": v(6.03, 11.42) * mm, "end": v(6.37, 11.53) * mm});
            skLineSegment(sketch, "E46.14.7.0", {"start": v(7.87, 12.67) * mm, "end": v(6.53, 10.51) * mm});
            skArc(sketch, "E46.17.7.0", {"start": v(8, 9.45) * mm, "mid": v(7.28, 10) * mm, "end": v(6.53, 10.51) * mm});
            skLineSegment(sketch, "E46.21.7.0", {"start": v(9.02, 10.47) * mm, "end": v(8, 9.45) * mm});
            skArc(sketch, "E46.24.7.0", {"start": v(9.02, 10.47) * mm, "mid": v(9.82, 10.66) * mm, "end": v(10.49, 11.14) * mm});
            skArc(sketch, "E46.28.7.0", {"start": v(11.07, 10.42) * mm, "mid": v(11.12, 11.11) * mm, "end": v(10.42, 11.08) * mm});
            skArc(sketch, "E46.32.7.0", {"start": v(10.47, 9.02) * mm, "mid": v(10.66, 9.82) * mm, "end": v(11.14, 10.49) * mm});
            skLineSegment(sketch, "E46.36.7.0", {"start": v(10.47, 9.02) * mm, "end": v(9.44, 8) * mm});
            skArc(sketch, "E46.39.7.0", {"start": v(9.44, 8) * mm, "mid": v(10, 7.28) * mm, "end": v(10.51, 6.53) * mm});
            skLineSegment(sketch, "E46.43.7.0", {"start": v(12.67, 7.87) * mm, "end": v(10.5, 6.54) * mm});
            skArc(sketch, "E46.46.7.0", {"start": v(11.77, 5.92) * mm, "mid": v(11.42, 6.03) * mm, "end": v(11.53, 6.37) * mm});
            skArc(sketch, "E46.50.7.0", {"start": v(12.3, 6.78) * mm, "mid": v(12.65, 6.69) * mm, "end": v(12.55, 6.34) * mm});
            skLineSegment(sketch, "E46.54.7.0", {"start": v(12.55, 6.34) * mm, "end": v(11.77, 5.92) * mm});
            skLineSegment(sketch, "E46.57.7.0", {"start": v(12.33, 6.8) * mm, "end": v(11.53, 6.37) * mm});
            skLineSegment(sketch, "E46.60.7.0", {"start": v(12.67, 7.87) * mm, "end": v(14.77, 12.03) * mm});
            skLineSegment(sketch, "E46.63.7.0", {"start": v(12.03, 14.77) * mm, "end": v(14.77, 12.03) * mm});
            skLineSegment(sketch, "E46.66.7.0", {"start": v(7.87, 12.67) * mm, "end": v(12.03, 14.77) * mm});
            skSolve(sketch);
        }
        {
            var Q0;
            {var subQ5=sQuery(id+"F4.wireOp",EDGE,"E25");Q0=makeQuery(id+"F4.imprint","IMPRINT",FACE,{"disambiguationData":[TD([[makeQuery(id+"F4.imprint","IMPRINT",EDGE,{"derivedFrom":subQ5}),1.0]])]});}
            var Q1;
            {var subQ5=sQuery(id+"F4.wireOp",EDGE,"E45.1.13");Q1=makeQuery(id+"F4.imprint","IMPRINT",FACE,{"disambiguationData":[TD([[makeQuery(id+"F4.imprint","IMPRINT",EDGE,{"derivedFrom":subQ5}),-1.0]])]});}
            var Q2;
            {var subQ1=sQuery(id+"F4.wireOp",EDGE,"E17");Q2=makeQuery(id+"F4.imprint","IMPRINT",FACE,{"disambiguationData":[TD([[makeQuery(id+"F4.imprint","IMPRINT",EDGE,{"derivedFrom":subQ1}),-1.0]])]});}
            var Q3;
            {var subQ3=sQuery(id+"F4.wireOp",EDGE,"E31.MirrorCS");Q3=makeQuery(id+"F4.imprint","IMPRINT",FACE,{"disambiguationData":[TD([[makeQuery(id+"F4.imprint","IMPRINT",EDGE,{"derivedFrom":subQ3}),-1.0]])]});}
            var Q4;
            {var subQ5=sQuery(id+"F4.wireOp",EDGE,"E46.2.7.0");Q4=makeQuery(id+"F4.imprint","IMPRINT",FACE,{"disambiguationData":[TD([[makeQuery(id+"F4.imprint","IMPRINT",EDGE,{"derivedFrom":subQ5}),1.0]])]});}
            var Q5;
            {var subQ5=sQuery(id+"F4.wireOp",EDGE,"E45.1.0");Q5=makeQuery(id+"F4.imprint","IMPRINT",FACE,{"disambiguationData":[TD([[makeQuery(id+"F4.imprint","IMPRINT",EDGE,{"derivedFrom":subQ5}),1.0]])]});}
            var Q6;
            {var subQ5=sQuery(id+"F4.wireOp",EDGE,"E45.2.13");Q6=makeQuery(id+"F4.imprint","IMPRINT",FACE,{"disambiguationData":[TD([[makeQuery(id+"F4.imprint","IMPRINT",EDGE,{"derivedFrom":subQ5}),-1.0]])]});}
            var Q7;
            {var subQ5=sQuery(id+"F4.wireOp",EDGE,"E46.46.7.0");Q7=makeQuery(id+"F4.imprint","IMPRINT",FACE,{"disambiguationData":[TD([[makeQuery(id+"F4.imprint","IMPRINT",EDGE,{"derivedFrom":subQ5}),-1.0]])]});}
            var Q8;
            {var subQ5=sQuery(id+"F4.wireOp",EDGE,"E46.2.6.0");Q8=makeQuery(id+"F4.imprint","IMPRINT",FACE,{"disambiguationData":[TD([[makeQuery(id+"F4.imprint","IMPRINT",EDGE,{"derivedFrom":subQ5}),1.0]])]});}
            var Q9;
            {var subQ5=sQuery(id+"F4.wireOp",EDGE,"E46.46.6.0");Q9=makeQuery(id+"F4.imprint","IMPRINT",FACE,{"disambiguationData":[TD([[makeQuery(id+"F4.imprint","IMPRINT",EDGE,{"derivedFrom":subQ5}),-1.0]])]});}
            var Q10;
            {var subQ5=sQuery(id+"F4.wireOp",EDGE,"E46.2.5.0");Q10=makeQuery(id+"F4.imprint","IMPRINT",FACE,{"disambiguationData":[TD([[makeQuery(id+"F4.imprint","IMPRINT",EDGE,{"derivedFrom":subQ5}),1.0]])]});}
            var Q11;
            {var subQ5=sQuery(id+"F4.wireOp",EDGE,"E46.46.5.0");Q11=makeQuery(id+"F4.imprint","IMPRINT",FACE,{"disambiguationData":[TD([[makeQuery(id+"F4.imprint","IMPRINT",EDGE,{"derivedFrom":subQ5}),-1.0]])]});}
            var Q12;
            {var subQ5=sQuery(id+"F4.wireOp",EDGE,"E46.2.4.0");Q12=makeQuery(id+"F4.imprint","IMPRINT",FACE,{"disambiguationData":[TD([[makeQuery(id+"F4.imprint","IMPRINT",EDGE,{"derivedFrom":subQ5}),1.0]])]});}
            var Q13;
            {var subQ5=sQuery(id+"F4.wireOp",EDGE,"E46.46.4.0");Q13=makeQuery(id+"F4.imprint","IMPRINT",FACE,{"disambiguationData":[TD([[makeQuery(id+"F4.imprint","IMPRINT",EDGE,{"derivedFrom":subQ5}),-1.0]])]});}
            var Q14;
            {var subQ5=sQuery(id+"F4.wireOp",EDGE,"E46.2.3.0");Q14=makeQuery(id+"F4.imprint","IMPRINT",FACE,{"disambiguationData":[TD([[makeQuery(id+"F4.imprint","IMPRINT",EDGE,{"derivedFrom":subQ5}),1.0]])]});}
            var Q15;
            {var subQ5=sQuery(id+"F4.wireOp",EDGE,"E46.46.3.0");Q15=makeQuery(id+"F4.imprint","IMPRINT",FACE,{"disambiguationData":[TD([[makeQuery(id+"F4.imprint","IMPRINT",EDGE,{"derivedFrom":subQ5}),-1.0]])]});}
            var Q16;
            {var subQ5=sQuery(id+"F4.wireOp",EDGE,"E45.2.0");Q16=makeQuery(id+"F4.imprint","IMPRINT",FACE,{"disambiguationData":[TD([[makeQuery(id+"F4.imprint","IMPRINT",EDGE,{"derivedFrom":subQ5}),1.0]])]});}
            extrude(context, id + "F5", {"entities" : qUnion([Q0, Q1, Q2, Q3, Q4, Q5, Q6, Q7, Q8, Q9, Q10, Q11, Q12, Q13, Q14, Q15, Q16]), "operationType" : NewBodyOperationType.ADD, "depth" : 0.76 * mm});
        }
    });
